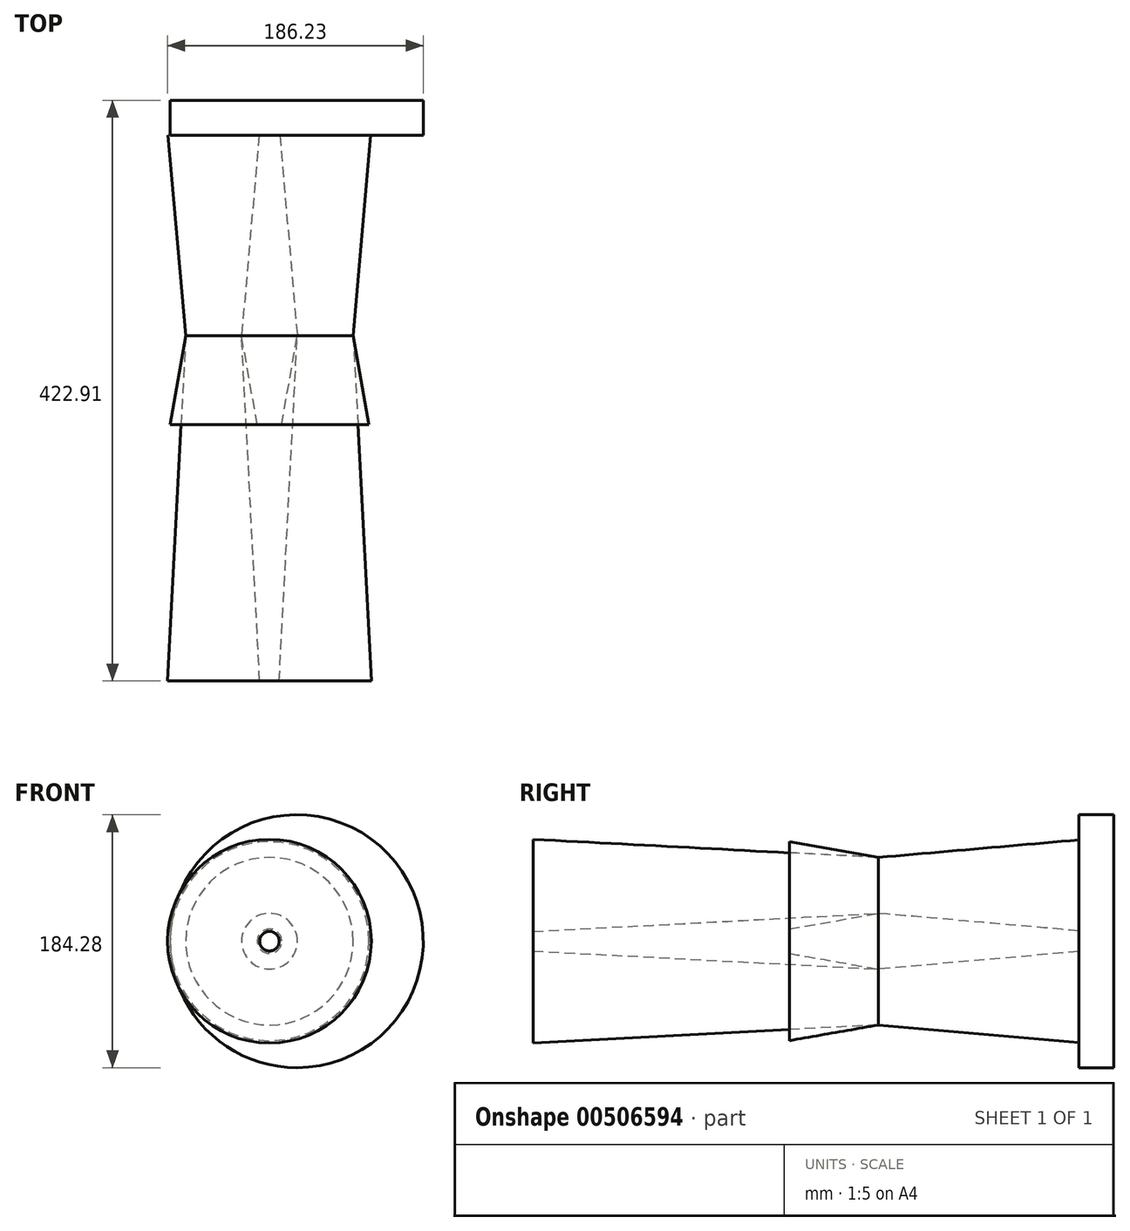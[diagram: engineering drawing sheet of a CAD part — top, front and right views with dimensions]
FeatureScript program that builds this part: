
annotation { "Feature Type Name" : "Feature", "Feature Type Description" : "" }
export const myFeature = defineFeature(function(context is Context, id is Id, definition is map)
    precondition{}
    {
        {
            var Q0;
            Q0=qCreatedBy(makeId("Front.planeOp"),FACE);
            var sketch = newSketch(context, id + "F0", { "sketchPlane" : qUnion([Q0])});
            skCircle(sketch, "E0", {"center": v(0, 0) * mm, "radius": 92.14 * mm});
            skSolve(sketch);
        }
        {
            var Q0;
            Q0 = qSketchRegion(id + "F0", true);
            extrude(context, id + "F1", {"entities" : qUnion([Q0]), "depth" : 25.4 * mm});
        }
        {
            var Q0;
            Q0=makeQuery(id+"F1.opExtrude","CAP_FACE",FACE,{"disambiguationData":[OSD([sQuery(id+"F0.wireOp",EDGE,"E0")])],"isStart":false});
            cPlane(context, id + "F2", {"entities" : qUnion([Q0]), "cplaneType" : CPlaneType.OFFSET, "offset" : 146.05 * mm, "width" : 152.4 * mm, "height" : 152.4 * mm});
        }
        {
            var Q0;
            Q0=qCreatedBy(id+"F2.planeOp",FACE);
            var sketch = newSketch(context, id + "F3", { "sketchPlane" : qUnion([Q0])});
            skCircle(sketch, "E1", {"center": v(-19.89, 0) * mm, "radius": 61.02 * mm});
            skCircle(sketch, "E2", {"center": v(-19.89, 0) * mm, "radius": 20.3 * mm});
            skSolve(sketch);
        }
        {
            var Q0;
            Q0=makeQuery(id+"F3.imprint","IMPRINT",FACE,{"disambiguationData":[TD([[makeQuery(id+"F3.imprint","IMPRINT",EDGE,{"derivedFrom":sQuery(id+"F3.wireOp",EDGE,"E1")}),1.0]])]});
            extrude(context, id + "F4", {"entities" : qUnion([Q0]), "depth" : 64.77 * mm, "hasDraft" : true, "draftAngle" : 10 * degree});
        }
        {
            var Q0;
            Q0=makeQuery(id+"F1.opExtrude","CAP_FACE",FACE,{"disambiguationData":[OSD([sQuery(id+"F0.wireOp",EDGE,"E0")])],"isStart":false});
            var sketch = newSketch(context, id + "F5", { "sketchPlane" : qUnion([Q0])});
            skSolve(sketch);
        }
        {
            var Q0;
            Q0 = qSketchRegion(id + "F5", true);
            var Q1;
            Q1=makeQuery(id+"F4.opExtrude","CAP_FACE",FACE,{"disambiguationData":[OSD([sQuery(id+"F3.wireOp",EDGE,"E1"),sQuery(id+"F3.wireOp",EDGE,"E2")])],"isStart":true});
            var Q2;
            Q2=makeQuery(id+"F1.opExtrude","CAP_FACE",FACE,{"disambiguationData":[OSD([sQuery(id+"F0.wireOp",EDGE,"E0")])],"isStart":false});
            extrude(context, id + "F6", {"entities" : qUnion([Q0, Q1]), "endBound" : BoundingType.UP_TO_SURFACE, "endBoundEntityFace" : qUnion([Q2]), "depth" : 25.4 * mm, "hasDraft" : true, "draftAngle" : 5 * degree, "hasSecondDirection" : true, "secondDirectionOppositeDirection" : true, "secondDirectionDepth" : 251.46 * mm, "hasSecondDirectionDraft" : true, "secondDirectionDraftAngle" : 3 * degree});
        }
    });
